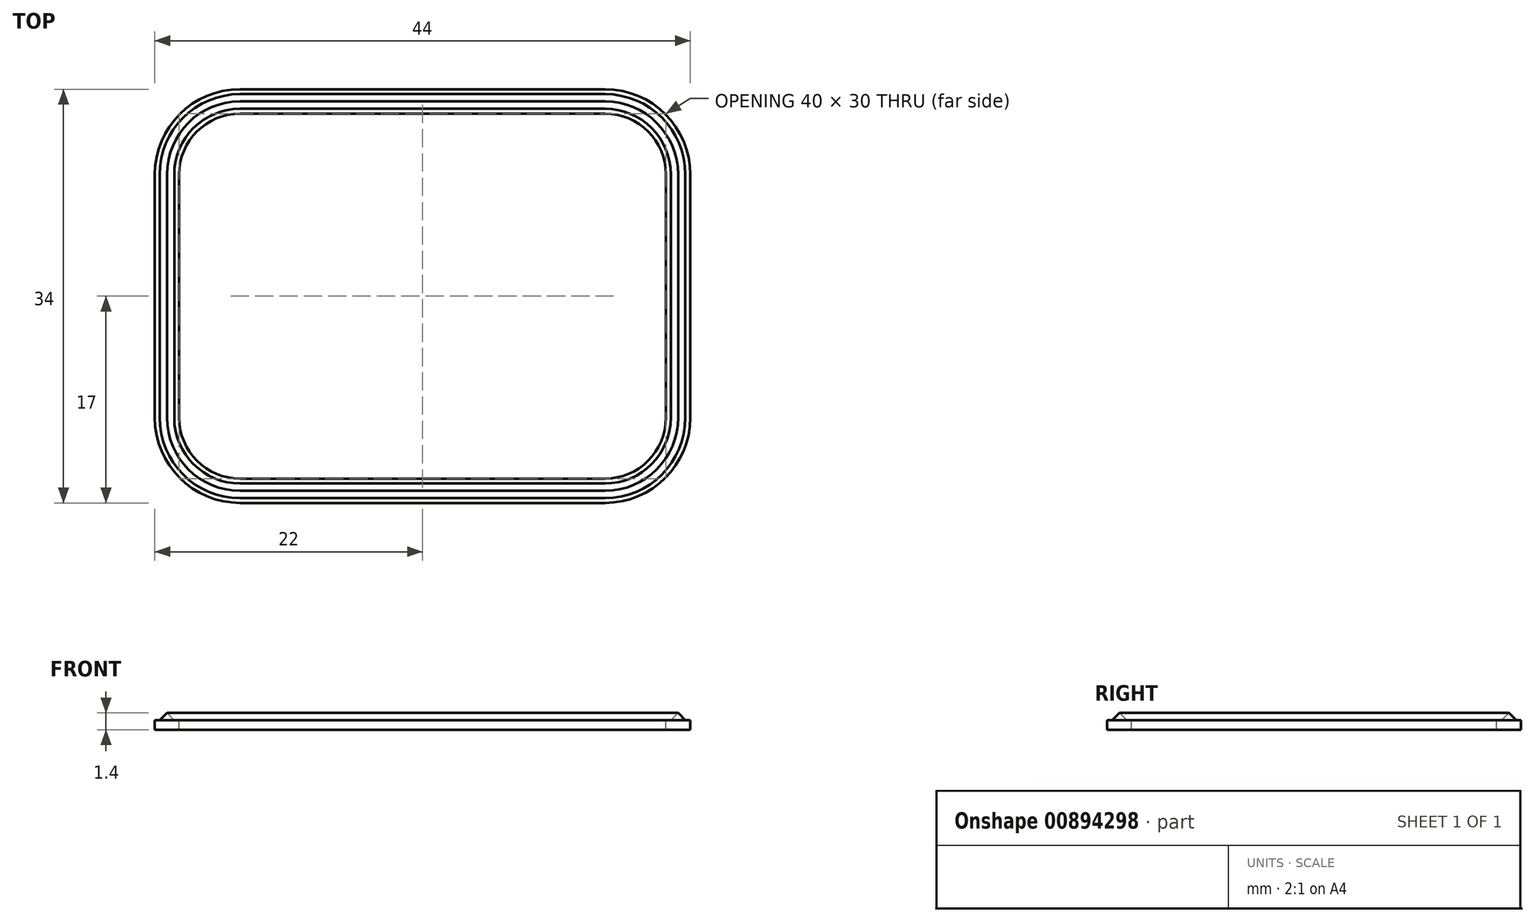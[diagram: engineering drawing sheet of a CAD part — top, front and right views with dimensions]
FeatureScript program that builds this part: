
annotation { "Feature Type Name" : "Feature", "Feature Type Description" : "" }
export const myFeature = defineFeature(function(context is Context, id is Id, definition is map)
    precondition{}
    {
        {
            var Q0;
            Q0=qCreatedBy(makeId("Top.planeOp"),FACE);
            var sketch = newSketch(context, id + "F0", { "sketchPlane" : qUnion([Q0])});
            skLineSegment(sketch, "E0.bottom", {"start": v(5, 0) * mm, "end": v(35, 0) * mm});
            skLineSegment(sketch, "E0.top", {"start": v(5, 30) * mm, "end": v(35, 30) * mm});
            skLineSegment(sketch, "E0.left", {"start": v(0, 5) * mm, "end": v(0, 25) * mm});
            skLineSegment(sketch, "E0.right", {"start": v(40, 5) * mm, "end": v(40, 25) * mm});
            skPoint(sketch, "E1.visualSharp", {"position": v(0, 30) * mm});
            skArc(sketch, "E1.filletArc", {"start": v(5, 30) * mm, "mid": v(1.46, 28.54) * mm, "end": v(0, 25) * mm});
            skPoint(sketch, "E2.visualSharp", {"position": v(40, 30) * mm});
            skArc(sketch, "E2.filletArc", {"start": v(40, 25) * mm, "mid": v(38.54, 28.54) * mm, "end": v(35, 30) * mm});
            skPoint(sketch, "E3.visualSharp", {"position": v(40, 0) * mm});
            skArc(sketch, "E3.filletArc", {"start": v(35, 0) * mm, "mid": v(38.54, 1.46) * mm, "end": v(40, 5) * mm});
            skPoint(sketch, "E4.visualSharp", {"position": v(0, 0) * mm});
            skArc(sketch, "E4.filletArc", {"start": v(0, 5) * mm, "mid": v(1.46, 1.46) * mm, "end": v(5, 0) * mm});
            skPoint(sketch, "E5", {"position": v(20, 0) * mm});
            skSolve(sketch);
        }
        {
            var Q0;
            Q0=sQuery(id+"F0.wireOp",EDGE,"E0.bottom");
            cPoint(context, id + "F1", {"entities" : qUnion([Q0]), "parameter" : 0.5});
        }
        {
            var Q0;
            Q0 = qCreatedBy(id + "F1" ,VERTEX);
            var Q1;
            Q1=sQuery(id+"F0.wireOp",EDGE,"E0.bottom");
            cPlane(context, id + "F2", {"entities" : qUnion([Q0, Q1]), "cplaneType" : CPlaneType.LINE_POINT, "offset" : 25 * mm, "width" : 150 * mm, "height" : 150 * mm});
        }
        {
            var Q0;
            Q0=qCreatedBy(id+"F2.planeOp",FACE);
            var sketch = newSketch(context, id + "F3", { "sketchPlane" : qUnion([Q0])});
            skLineSegment(sketch, "E6.bottom", {"start": v(0, 0) * mm, "end": v(-2, 0) * mm});
            skLineSegment(sketch, "E6.top", {"start": v(0, 0.8) * mm, "end": v(-0.4, 0.8) * mm});
            skLineSegment(sketch, "E6.left", {"start": v(0, 0) * mm, "end": v(0, 0.8) * mm});
            skLineSegment(sketch, "E6.right", {"start": v(-2, 0) * mm, "end": v(-2, 0.8) * mm});
            skLineSegment(sketch, "E7", {"start": v(-1, 0.8) * mm, "end": v(-1, 1.4) * mm, "construction": true});
            skLineSegment(sketch, "E8", {"start": v(-1, 1.4) * mm, "end": v(-1.6, 0.8) * mm});
            skLineSegment(sketch, "E9", {"start": v(-1, 1.4) * mm, "end": v(-0.4, 0.8) * mm});
            skLineSegment(sketch, "E10.trimOffspring", {"start": v(-1.6, 0.8) * mm, "end": v(-2, 0.8) * mm});
            skSolve(sketch);
        }
        {
            var Q0;
            Q0=makeQuery(id+"F3.imprint","IMPRINT",FACE,{"disambiguationData":[TD([[makeQuery(id+"F3.imprint","IMPRINT",EDGE,{"derivedFrom":sQuery(id+"F3.wireOp",EDGE,"E6.bottom")}),-1.0]])]});
            var Q1;
            Q1 = qConstructionFilter(qBodyType(qCreatedBy(id + "F0" ,EDGE), BodyType.WIRE), ConstructionObject.NO);
            sweep(context, id + "F4", {"profiles" : qUnion([Q0]), "path" : qUnion([Q1])});
        }
    });
